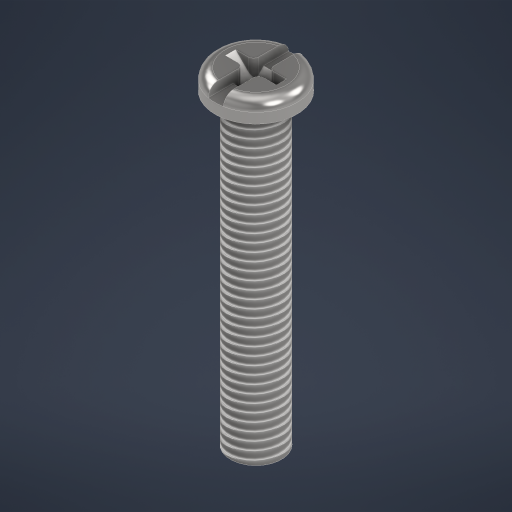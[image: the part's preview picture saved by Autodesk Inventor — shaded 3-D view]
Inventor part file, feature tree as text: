
AUTODESK INVENTOR PART (.ipt)
format: ipt  version: 2023.2 (Build 272271000, 271)  size: 347,136 bytes
history: native  units: mm
features: sketch x1, thread x1
ambient origin geometry x8: Origin, YZ Plane, XZ Plane, XY Plane, X Axis, Y Axis, Z Axis, Center Point
bodies: Body1 (feature_tree)
feature tree (2):
  sketch  "Sketch1"  dims[d229=8.0mm d230=30.0mm d231=0.0mm d232=2.0mm d233=0.0mm d234=8.0mm d235=1.5mm d236=1.0mm d237=5.0mm d238=5.0mm d239=1.0mm d240=0.0mm d243=1.0mm d244=1.0mm d245=2.0mm d246=0.0mm d247=2.0mm d248=2.0mm d249=45.0deg d257=2.0mm d258=0.0mm d259=30.0mm d260=0.0mm d264=0.5mm d265=1.0mm d266=0.5mm d9=0.5mm d10=0.872665mm d11=0.5mm d12=0.872665mm d13=0.5mm d14=0.872665mm d27=0.5mm d28=0.872665mm d29=0.5mm d30=0.872665mm d88=0.5mm d89=0.872665mm d90=0.5mm d91=0.872665mm d116=0.5mm d117=0.872665mm d118=0.5mm d119=0.872665mm d154=0.5mm d155=0.872665mm d156=0.5mm d157=0.872665mm d181=0.5mm d182=0.872665mm d183=0.5mm d184=0.872665mm d221=0.5mm d222=0.872665mm d223=0.5mm d224=0.872665mm d267=0.0mm d268=0.0mm d269=0.0mm d270=0.0mm]
  thread  "Thread1"  [1 undecoded]
note: 1 required parameter value undecoded (feature->parameter linkage not recoverable at this tier; creation-order binding heuristic only, values carry confidence <= 0.55)
